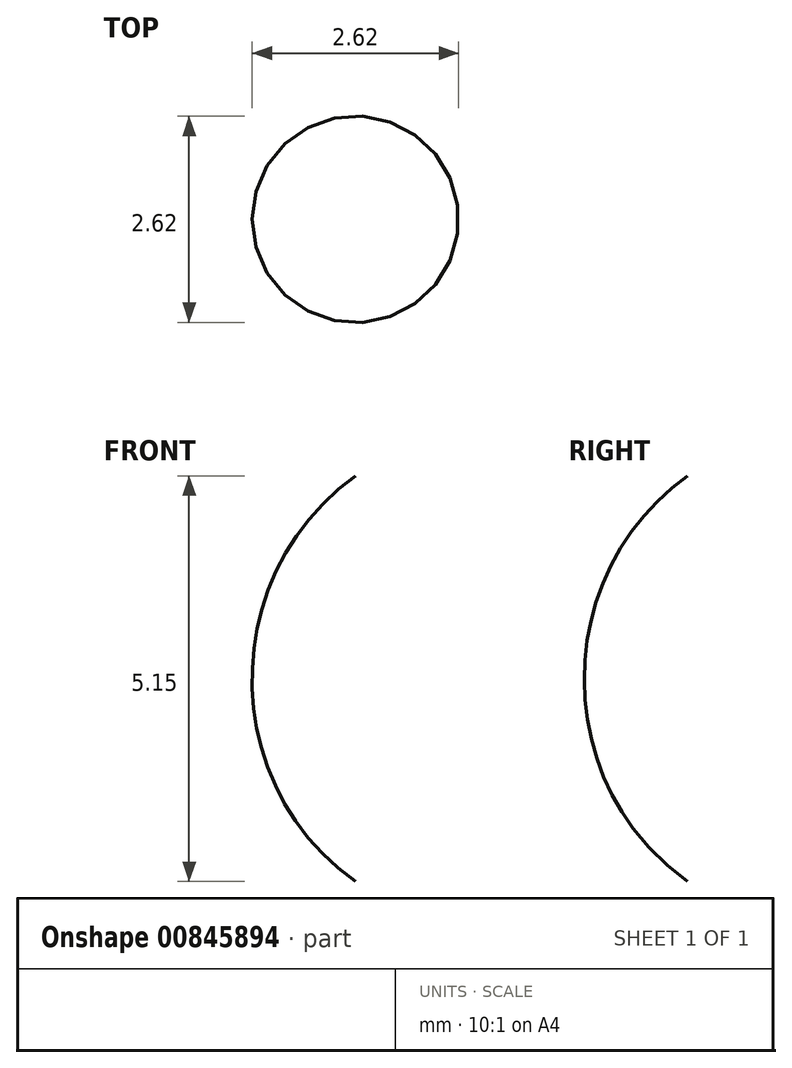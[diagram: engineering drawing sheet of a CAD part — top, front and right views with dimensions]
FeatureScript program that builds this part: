
annotation { "Feature Type Name" : "Feature", "Feature Type Description" : "" }
export const myFeature = defineFeature(function(context is Context, id is Id, definition is map)
    precondition{}
    {
        {
            var Q0;
            Q0=qCreatedBy(makeId("Front.planeOp"),FACE);
            var sketch = newSketch(context, id + "F0", { "sketchPlane" : qUnion([Q0])});
            skFitSpline(sketch, "E0", {"points": [v(24.66, 56.35) * mm, v(40, 48.27) * mm, v(49.49, 37.45) * mm, v(27.42, 0) * mm, v(18.86, 0) * mm, v(0, 0) * mm, v(0, 5.15) * mm, v(23.41, 6.71) * mm, v(41, 26.76) * mm, v(41.9, 37.58) * mm, v(20.3, 53.54) * mm, v(24.66, 56.35) * mm]});
            skLineSegment(sketch, "E1", {"start": v(0, 80.7) * mm, "end": v(0, -5.46) * mm});
            skSolve(sketch);
        }
        {
            var Q0;
            {var subQ0=sQuery(id+"F0.wireOp",EDGE,"E1");var subQ1=sQuery(id+"F0.wireOp",EDGE,"E0");var subQ2=makeQuery(id+"F0.imprint","INTERSECT",VERTEX,{"disambiguationData":[OD(0.0)],"derivedFrom":[subQ1,subQ0]});Q0=makeQuery(id+"F0.imprint","IMPRINT",FACE,{"disambiguationData":[TD([[makeQuery(id+"F0.imprint","IMPRINT",EDGE,{"disambiguationData":[TD([[subQ2,1.0]])],"derivedFrom":subQ1}),-1.0]])]});}
            var Q1;
            Q1=sQuery(id+"F0.wireOp",EDGE,"E1");
            revolve(context, id + "F1", {"surfaceOperationType" : NewSurfaceOperationType.NEW, "entities" : qUnion([Q0]), "axis" : qUnion([Q1]), "revolveType" : RevolveType.FULL});
        }
    });
